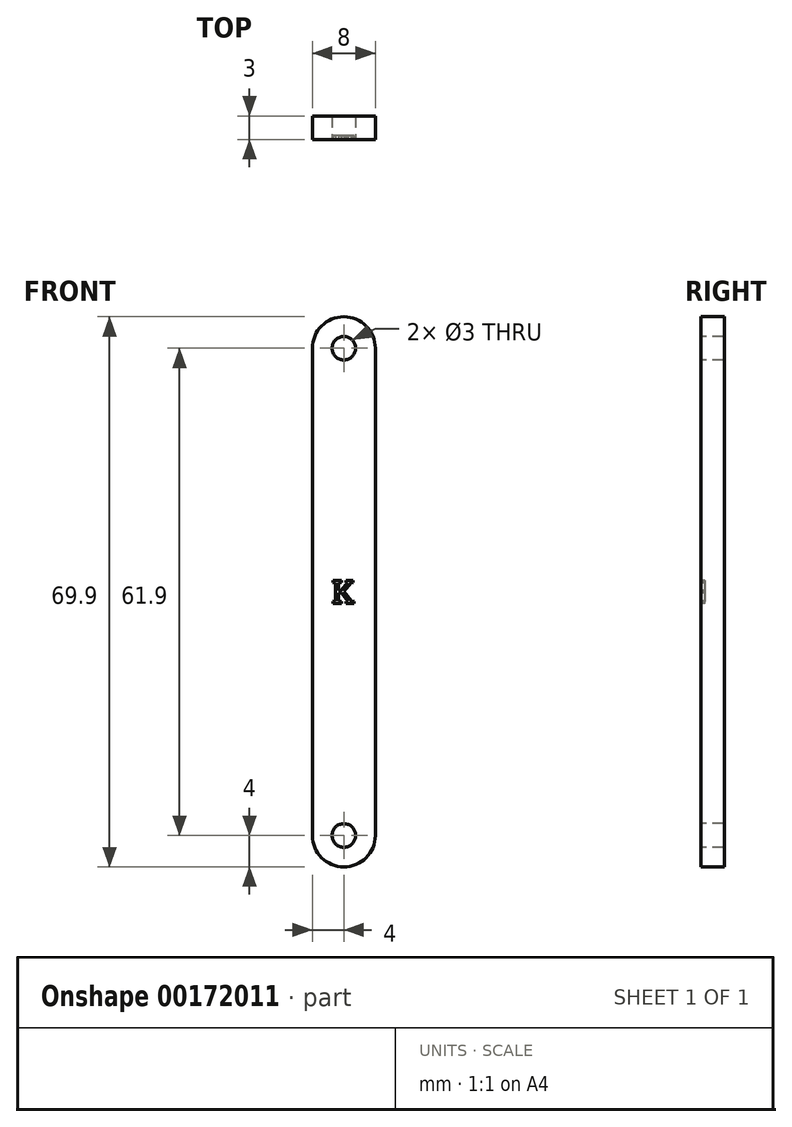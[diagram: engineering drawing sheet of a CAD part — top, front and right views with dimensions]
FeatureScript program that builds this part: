
annotation { "Feature Type Name" : "Feature", "Feature Type Description" : "" }
export const myFeature = defineFeature(function(context is Context, id is Id, definition is map)
    precondition{}
    {
        {
            assignVariable(context, id + "F0", {"name" : "Thickness", "anyValue" : 3});
        }
        {
            var Q0;
            Q0=qCreatedBy(makeId("Front.planeOp"),FACE);
            var sketch = newSketch(context, id + "F1", { "sketchPlane" : qUnion([Q0])});
            skCircle(sketch, "E0", {"center": v(0, 61.9) * mm, "radius": 1.5 * mm});
            skCircle(sketch, "E1", {"center": v(0, 0) * mm, "radius": 1.5 * mm});
            skArc(sketch, "E2", {"start": v(4, 61.9) * mm, "mid": v(0, 65.9) * mm, "end": v(-4, 61.9) * mm});
            skArc(sketch, "E3", {"start": v(-4, 0) * mm, "mid": v(0, -4) * mm, "end": v(4, 0) * mm});
            skLineSegment(sketch, "E4", {"start": v(-4, 0) * mm, "end": v(-4, 61.9) * mm});
            skLineSegment(sketch, "E5", {"start": v(4, 61.9) * mm, "end": v(4, 0) * mm});
            skSolve(sketch);
        }
        {
            var Q0;
            Q0=makeQuery(id+"F1.imprint","IMPRINT",FACE,{"disambiguationData":[TD([[makeQuery(id+"F1.imprint","IMPRINT",EDGE,{"derivedFrom":sQuery(id+"F1.wireOp",EDGE,"0kyrNfPp-UYAh-n8tk-IVnA-H5sSIWuTYwV2")}),-1.0]])]});
            var Q1;
            Q1=makeQuery(id+"F1.imprint","IMPRINT",FACE,{"disambiguationData":[TD([[makeQuery(id+"F1.imprint","IMPRINT",EDGE,{"derivedFrom":sQuery(id+"F1.wireOp",EDGE,"E0")}),-1.0]])]});
            extrude(context, id + "F2", {"entities" : qUnion([Q0, Q1]), "oppositeDirection" : true, "depth" : (getVariable(context, 'Thickness')) * mm});
        }
        {
            var Q0;
            Q0=qCreatedBy(makeId("Front.planeOp"),FACE);
            var sketch = newSketch(context, id + "F3", { "sketchPlane" : qUnion([Q0])});
            skText(sketch, "E6", { "text": "K", "fontName": "RobotoSlab-Regular.ttf"});
            skLineSegment(sketch, "E7", {"start": v(1.54, 30.95) * mm, "end": v(4, 30.95) * mm, "construction": true});
            const initialGuessF3  = {"E6": [-0.00154, 0.02945, 1, 0, 0.003]};
            skSetInitialGuess(sketch, initialGuessF3);
            skSolve(sketch);
        }
        {
            assignVariable(context, id + "F4", {"name" : "DepthText", "anyValue" : .5});
        }
        {
            var Q0;
            Q0=qSketchRegion(id+"F3",true);
            extrude(context, id + "F5", {"entities" : qUnion([Q0]), "operationType" : NewBodyOperationType.REMOVE, "oppositeDirection" : true, "depth" : (getVariable(context, 'DepthText')) * mm});
        }
    });
